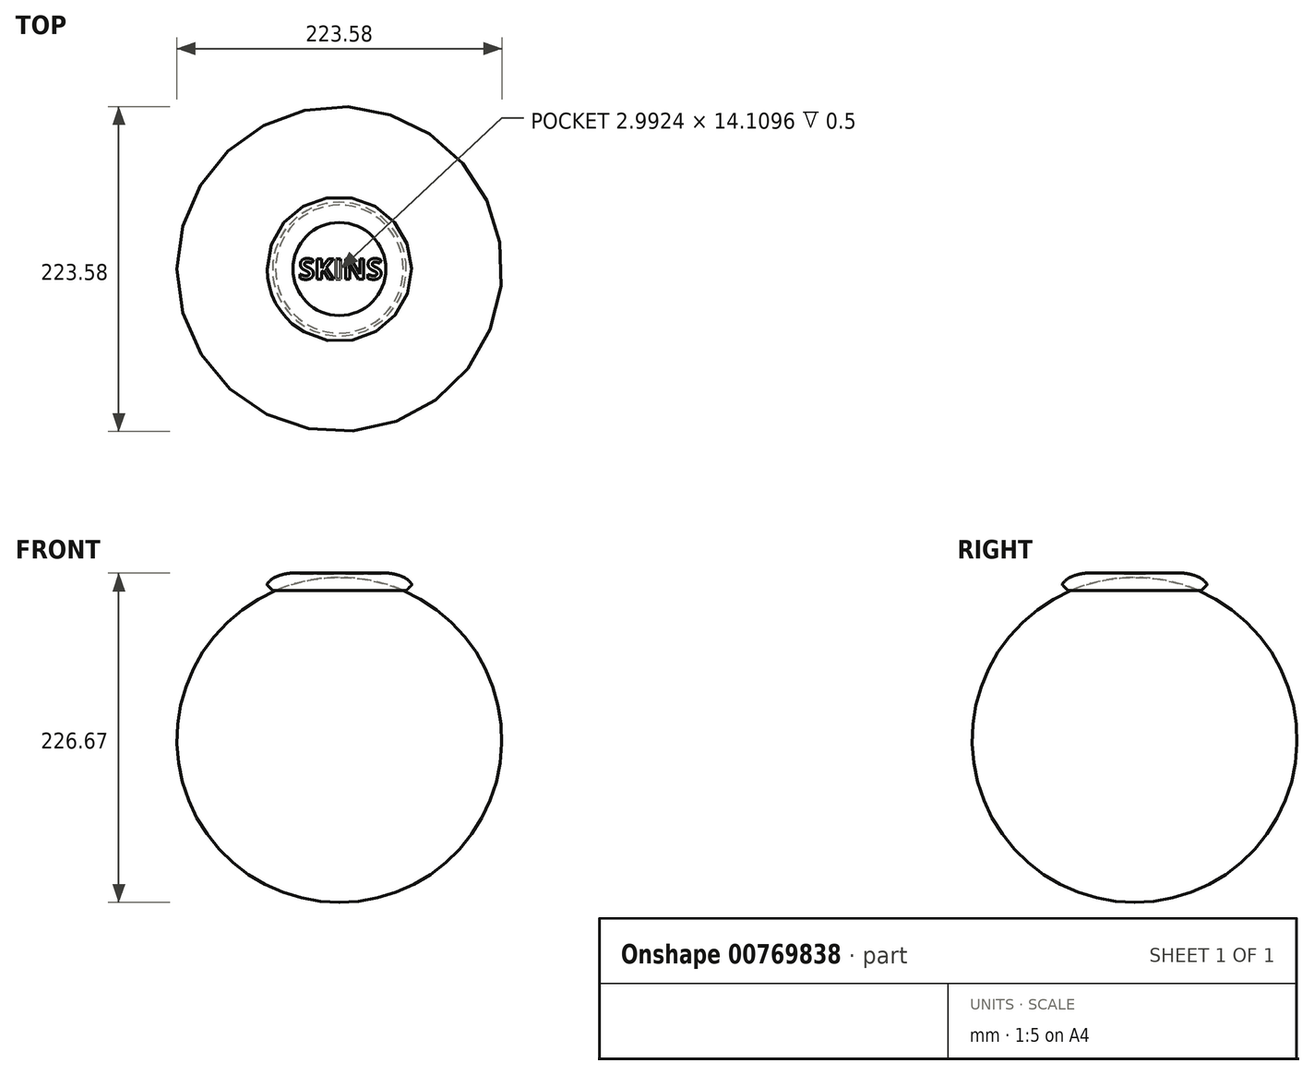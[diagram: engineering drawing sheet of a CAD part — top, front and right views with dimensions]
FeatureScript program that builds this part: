
annotation { "Feature Type Name" : "Feature", "Feature Type Description" : "" }
export const myFeature = defineFeature(function(context is Context, id is Id, definition is map)
    precondition{}
    {
        {
            var Q0;
            Q0=qCreatedBy(makeId("Top.planeOp"),FACE);
            var sketch = newSketch(context, id + "F0", { "sketchPlane" : qUnion([Q0])});
            skCircle(sketch, "E0", {"center": v(0, 0) * mm, "radius": 50 * mm});
            skSolve(sketch);
        }
        {
            var Q0;
            Q0=qSketchRegion(id+"F0",true);
            extrude(context, id + "F1", {"entities" : qUnion([Q0]), "depth" : 12 * mm, "offsetDistance" : 25 * mm});
        }
        {
            var Q0;
            Q0=makeQuery(id+"F1.opExtrude","CAP_FACE",FACE,{"disambiguationData":[OSD([sQuery(id+"F0.wireOp",EDGE,"E0")])],"isStart":true});
            chamfer(context, id + "F2", {"entities" : qUnion([Q0]), "width" : 4 * mm, "tangentPropagation" : true});
        }
        {
            var Q0;
            Q0=qCreatedBy(makeId("Front.planeOp"),FACE);
            var sketch = newSketch(context, id + "F3", { "sketchPlane" : qUnion([Q0])});
            skLineSegment(sketch, "E1", {"start": v(-32, 12) * mm, "end": v(-32, 25.16) * mm});
            skLineSegment(sketch, "E2", {"start": v(-41, 13.4) * mm, "end": v(-41, 24.79) * mm});
            skLineSegment(sketch, "E3", {"start": v(-50, 4) * mm, "end": v(-50, 25.02) * mm});
            skArc(sketch, "E4", {"start": v(-44.87, 8.8) * mm, "mid": v(-47.77, 6.75) * mm, "end": v(-50, 4) * mm});
            skArc(sketch, "E5", {"start": v(-32, 12) * mm, "mid": v(-38.62, 11.15) * mm, "end": v(-44.87, 8.8) * mm});
            skLineSegment(sketch, "E6", {"start": v(-54.4, 12) * mm, "end": v(-50, 12) * mm});
            skLineSegment(sketch, "E7", {"start": v(-50, 4) * mm, "end": v(-50, 12) * mm});
            skLineSegment(sketch, "E8", {"start": v(0, 10.8) * mm, "end": v(0, 54.2) * mm});
            skLineSegment(sketch, "E9", {"start": v(-50, 12) * mm, "end": v(-32, 12) * mm});
            skSolve(sketch);
        }
        {
            var Q0;
            Q0=qSketchRegion(id+"F3",true);
            var Q1;
            Q1=sQuery(id+"F3.wireOp",EDGE,"E8");
            revolve(context, id + "F4", {"operationType" : NewBodyOperationType.REMOVE, "surfaceOperationType" : NewSurfaceOperationType.NEW, "entities" : qUnion([Q0]), "axis" : qUnion([Q1]), "revolveType" : RevolveType.FULL, "oppositeDirection" : true});
        }
        {
            var Q0;
            Q0=makeQuery(id+"F1.opExtrude","CAP_FACE",FACE,{"disambiguationData":[OSD([sQuery(id+"F0.wireOp",EDGE,"E0")])],"isStart":false});
            var sketch = newSketch(context, id + "F5", { "sketchPlane" : qUnion([Q0])});
            skText(sketch, "E10", { "text": "SKINS", "fontName": "OpenSans-Bold.ttf"});
            const initialGuessF5  = {"E10": [-0.028, -0.007, 1, 0, 0.01423]};
            skSetInitialGuess(sketch, initialGuessF5);
            skSolve(sketch);
        }
        {
            var Q0;
            Q0=qSketchRegion(id+"F5",true);
            extrude(context, id + "F6", {"entities" : qUnion([Q0]), "operationType" : NewBodyOperationType.REMOVE, "oppositeDirection" : true, "depth" : .5 * mm, "offsetDistance" : 25 * mm});
        }
        {
            var Q0;
            Q0=qCreatedBy(makeId("Front.planeOp"),FACE);
            var sketch = newSketch(context, id + "F7", { "sketchPlane" : qUnion([Q0])});
            skLineSegment(sketch, "E11", {"start": v(0, 0) * mm, "end": v(0, 9) * mm});
            skLineSegment(sketch, "E12", {"start": v(-44, 0) * mm, "end": v(0, 0) * mm});
            skLineSegment(sketch, "E13", {"start": v(0, -25.26) * mm, "end": v(0, -4.86) * mm});
            skArc(sketch, "E14", {"start": v(0, 9) * mm, "mid": v(-22.46, 6.73) * mm, "end": v(-44, 0) * mm});
            skSolve(sketch);
        }
        {
            var Q0;
            Q0=qSketchRegion(id+"F7",true);
            var Q1;
            Q1=sQuery(id+"F7.wireOp",EDGE,"E13");
            revolve(context, id + "F8", {"operationType" : NewBodyOperationType.REMOVE, "surfaceOperationType" : NewSurfaceOperationType.NEW, "entities" : qUnion([Q0]), "axis" : qUnion([Q1]), "revolveType" : RevolveType.FULL, "oppositeDirection" : true});
        }
        {
            var Q0;
            {var subQ0=sQuery(id+"F0.wireOp",EDGE,"E0");Q0=makeQuery(id+"F4.boolean.opBoolean","MERGE",EDGE,{"derivedFrom":[makeQuery(id+"F2.opChamfer","BLEND_EDGE",EDGE,{"blendedFrom":[makeQuery(id+"F1.opExtrude","CAP_EDGE",EDGE,{"disambiguationData":[OSD([subQ0])],"isStart":true}),makeQuery(id+"F1.opExtrude","SWEPT_FACE",FACE,{"disambiguationData":[OSD([subQ0])]})],"blendedInto":[makeQuery(id+"F1.opExtrude","SWEPT_FACE",FACE,{"disambiguationData":[OSD([subQ0])]})]}),makeQuery(id+"F4.opRevolve","SWEPT_EDGE",EDGE,{"disambiguationData":[OSD([sQuery(id+"F3.wireOp",EDGE,"E4"),sQuery(id+"F3.wireOp",EDGE,"E7")])]})]});}
            fillet(context, id + "F9", {"entities" : qUnion([Q0]), "radius" : 1 * mm, "tangentPropagation" : true, "allowEdgeOverflow" : false});
        }
    });
